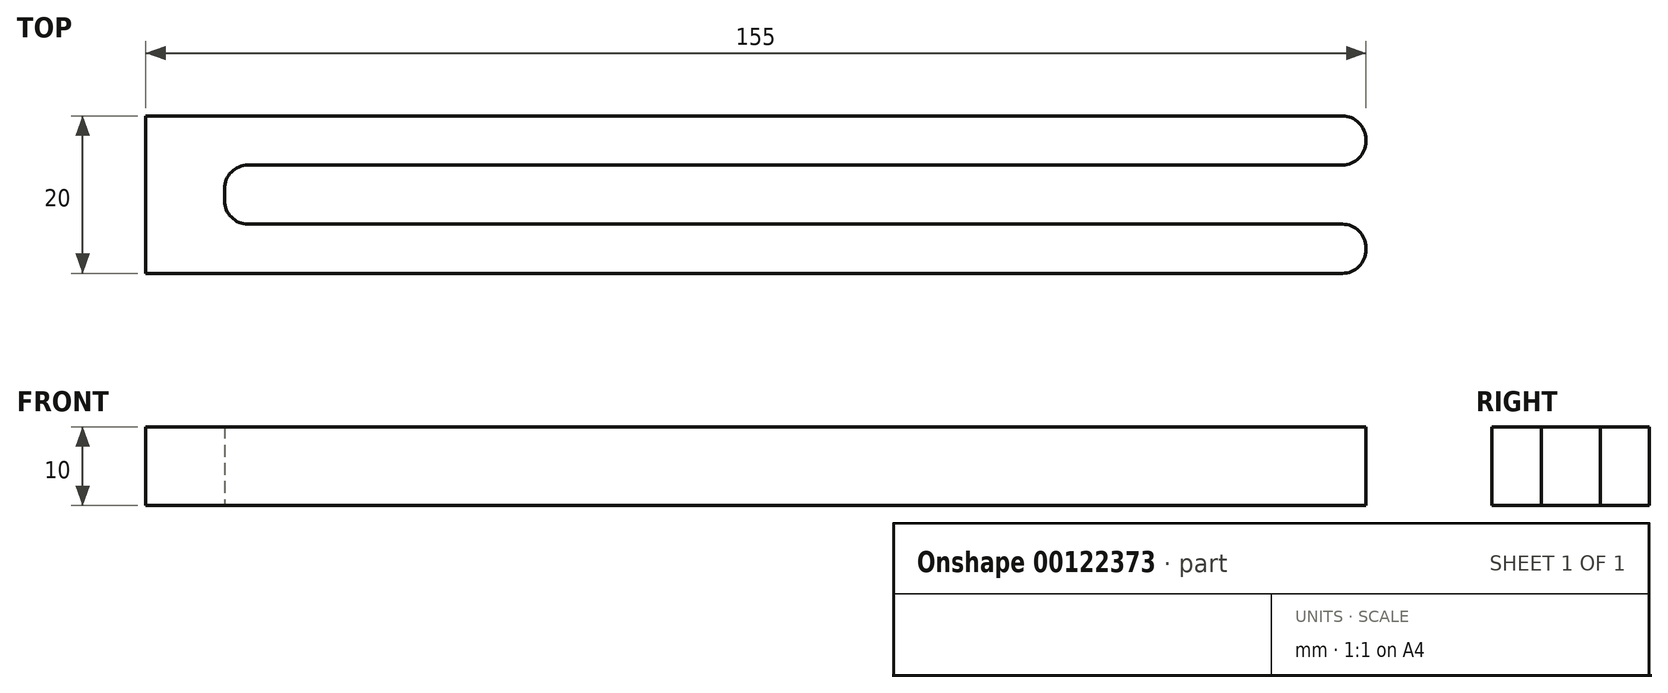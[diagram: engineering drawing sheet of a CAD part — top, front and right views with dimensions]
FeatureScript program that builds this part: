
annotation { "Feature Type Name" : "Feature", "Feature Type Description" : "" }
export const myFeature = defineFeature(function(context is Context, id is Id, definition is map)
    precondition{}
    {
        {
            var Q0;
            Q0=qCreatedBy(makeId("Top.planeOp"),FACE);
            var sketch = newSketch(context, id + "F0", { "sketchPlane" : qUnion([Q0])});
            skLineSegment(sketch, "E0.bottom", {"start": v(74.5, -10) * mm, "end": v(-77.5, -10) * mm});
            skLineSegment(sketch, "E0.top", {"start": v(74.5, 10) * mm, "end": v(-77.5, 10) * mm});
            skLineSegment(sketch, "E0.left", {"start": v(77.5, -7) * mm, "end": v(77.5, -6.75) * mm});
            skLineSegment(sketch, "E0.right", {"start": v(-77.5, -10) * mm, "end": v(-77.5, 10) * mm});
            skPoint(sketch, "E0.middle", {"position": v(0, 0) * mm});
            skLineSegment(sketch, "E1", {"start": v(74.5, 3.75) * mm, "end": v(-64.5, 3.75) * mm});
            skLineSegment(sketch, "E2", {"start": v(-67.5, 0.75) * mm, "end": v(-67.5, -0.75) * mm});
            skLineSegment(sketch, "E3", {"start": v(-64.5, -3.75) * mm, "end": v(74.5, -3.75) * mm});
            skLineSegment(sketch, "E4.trimOffspring", {"start": v(77.5, 6.75) * mm, "end": v(77.5, 7) * mm});
            skPoint(sketch, "E5.visualSharp", {"position": v(77.5, 10) * mm});
            skArc(sketch, "E5.filletArc", {"start": v(77.5, 7) * mm, "mid": v(76.62, 9.12) * mm, "end": v(74.5, 10) * mm});
            skPoint(sketch, "E6.visualSharp", {"position": v(77.5, 3.75) * mm});
            skArc(sketch, "E6.filletArc", {"start": v(74.5, 3.75) * mm, "mid": v(76.62, 4.63) * mm, "end": v(77.5, 6.75) * mm});
            skPoint(sketch, "E7.visualSharp", {"position": v(77.5, -3.75) * mm});
            skArc(sketch, "E7.filletArc", {"start": v(77.5, -6.75) * mm, "mid": v(76.62, -4.63) * mm, "end": v(74.5, -3.75) * mm});
            skPoint(sketch, "E8.visualSharp", {"position": v(77.5, -10) * mm});
            skArc(sketch, "E8.filletArc", {"start": v(74.5, -10) * mm, "mid": v(76.62, -9.12) * mm, "end": v(77.5, -7) * mm});
            skPoint(sketch, "E9.visualSharp", {"position": v(-67.5, 3.75) * mm});
            skArc(sketch, "E9.filletArc", {"start": v(-64.5, 3.75) * mm, "mid": v(-66.62, 2.87) * mm, "end": v(-67.5, 0.75) * mm});
            skPoint(sketch, "E10.visualSharp", {"position": v(-67.5, -3.75) * mm});
            skArc(sketch, "E10.filletArc", {"start": v(-67.5, -0.75) * mm, "mid": v(-66.62, -2.87) * mm, "end": v(-64.5, -3.75) * mm});
            skSolve(sketch);
        }
        {
            var Q0;
            Q0 = qSketchRegion(id + "F0", true);
            extrude(context, id + "F1", {"entities" : qUnion([Q0]), "depth" : 10 * mm});
        }
    });
